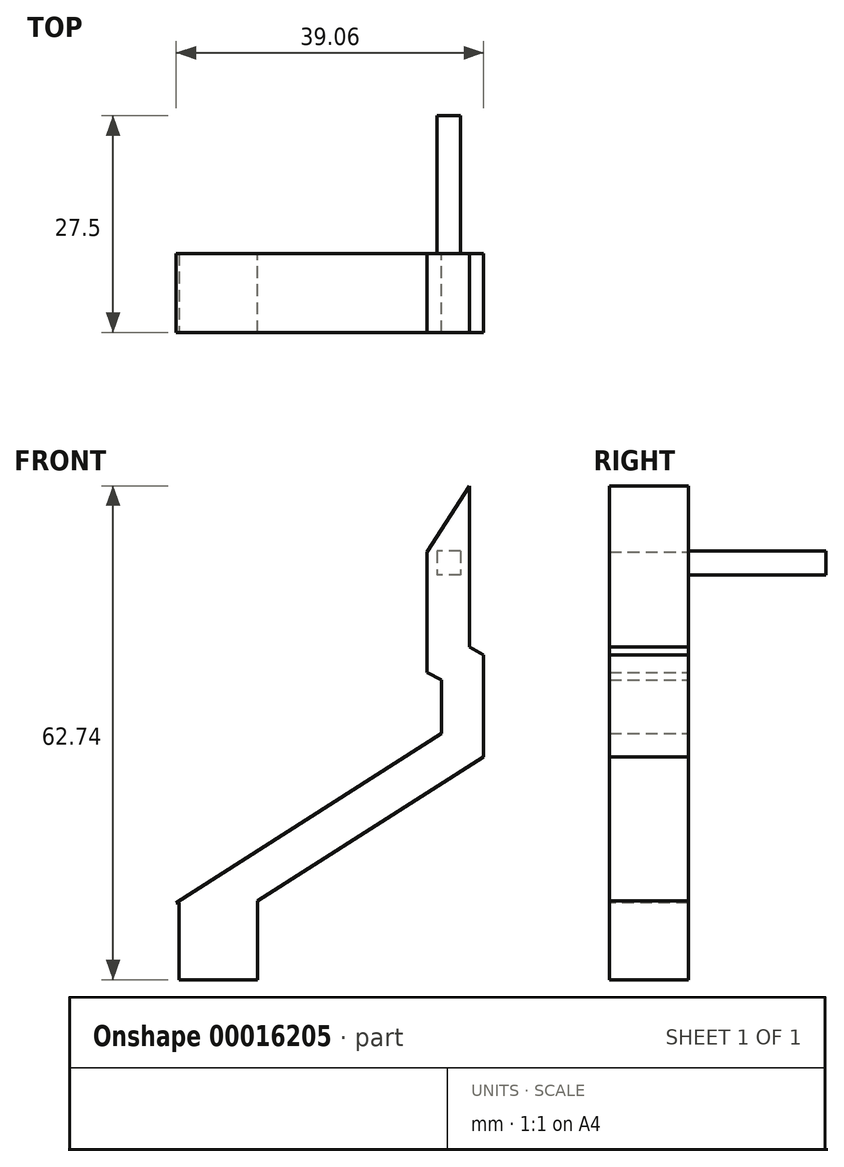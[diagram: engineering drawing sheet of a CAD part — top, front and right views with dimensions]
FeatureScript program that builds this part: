
annotation { "Feature Type Name" : "Feature", "Feature Type Description" : "" }
export const myFeature = defineFeature(function(context is Context, id is Id, definition is map)
    precondition{}
    {
        {
            var Q0;
            Q0=qCreatedBy(makeId("Right.planeOp"),FACE);
            var sketch = newSketch(context, id + "F0", { "sketchPlane" : qUnion([Q0])});
            skLineSegment(sketch, "E0.bottom", {"start": v(-13.57, -10.67) * mm, "end": v(-3.57, -10.67) * mm});
            skLineSegment(sketch, "E0.top", {"start": v(-13.57, -20.67) * mm, "end": v(-3.57, -20.67) * mm});
            skLineSegment(sketch, "E0.left", {"start": v(-13.57, -10.67) * mm, "end": v(-13.57, -20.67) * mm});
            skLineSegment(sketch, "E0.right", {"start": v(-3.57, -10.67) * mm, "end": v(-3.57, -20.67) * mm});
            skSolve(sketch);
        }
        {
            var Q0;
            Q0=makeQuery(id+"F0.imprint","IMPRINT",FACE,{"disambiguationData":[TD([[makeQuery(id+"F0.imprint","IMPRINT",EDGE,{"derivedFrom":sQuery(id+"F0.wireOp",EDGE,"E0.bottom")}),-1.0]])]});
            extrude(context, id + "F1", {"entities" : qUnion([Q0]), "depth" : 10 * mm});
        }
        {
            var Q0;
            Q0=makeQuery(id+"F1.opExtrude","SWEPT_FACE",FACE,{"disambiguationData":[OSD([sQuery(id+"F0.wireOp",EDGE,"E0.bottom")])]});
            var sketch = newSketch(context, id + "F2", { "sketchPlane" : qUnion([Q0])});
            skLineSegment(sketch, "E1.bottom", {"start": v(0, -3.57) * mm, "end": v(10, -3.57) * mm});
            skLineSegment(sketch, "E1.top", {"start": v(0, -13.57) * mm, "end": v(10, -13.57) * mm});
            skLineSegment(sketch, "E1.left", {"start": v(0, -3.57) * mm, "end": v(0, -13.57) * mm});
            skLineSegment(sketch, "E1.right", {"start": v(10, -3.57) * mm, "end": v(10, -13.57) * mm});
            skSolve(sketch);
        }
        {
            var Q0;
            Q0=qCreatedBy(makeId("Front.planeOp"),FACE);
            var sketch = newSketch(context, id + "F3", { "sketchPlane" : qUnion([Q0])});
            skLineSegment(sketch, "E2", {"start": v(4.82, -10.91) * mm, "end": v(36.1, 9.06) * mm});
            skLineSegment(sketch, "E3", {"start": v(36.1, 9.06) * mm, "end": v(36.1, 19.06) * mm});
            skLineSegment(sketch, "E4", {"start": v(36.1, 19.06) * mm, "end": v(34.3, 20.02) * mm});
            skLineSegment(sketch, "E5", {"start": v(34.3, 20.02) * mm, "end": v(34.3, 38.02) * mm});
            skSolve(sketch);
        }
        {
            var Q0;
            Q0=makeQuery(id+"F2.imprint","IMPRINT",FACE,{"disambiguationData":[TD([[makeQuery(id+"F2.imprint","IMPRINT",EDGE,{"derivedFrom":sQuery(id+"F2.wireOp",EDGE,"E1.bottom")}),1.0]])]});
            var Q1;
            Q1=sQuery(id+"F3.wireOp",EDGE,"E5");
            var Q2;
            Q2=sQuery(id+"F3.wireOp",EDGE,"E2");
            var Q3;
            Q3=sQuery(id+"F3.wireOp",EDGE,"E4");
            var Q4;
            Q4=sQuery(id+"F3.wireOp",EDGE,"E3");
            sweep(context, id + "F4", {"operationType" : NewBodyOperationType.ADD, "profiles" : qUnion([Q0]), "path" : qUnion([Q1, Q2, Q3, Q4])});
        }
        {
            var Q0;
            Q0=makeQuery(id+"F4.boolean.opBoolean","MERGE",FACE,{"derivedFrom":[makeQuery(id+"F1.opExtrude","SWEPT_FACE",FACE,{"disambiguationData":[OSD([sQuery(id+"F0.wireOp",EDGE,"E0.right")])]}),makeQuery(id+"F4.opSweep","SWEPT_FACE",FACE,{"disambiguationData":[OSD([sQuery(id+"F2.wireOp",EDGE,"E1.bottom"),sQuery(id+"F3.wireOp",EDGE,"E2")])]})]});
            var sketch = newSketch(context, id + "F5", { "sketchPlane" : qUnion([Q0])});
            skLineSegment(sketch, "E6.bottom", {"start": v(-35.78, 33.77) * mm, "end": v(-32.78, 33.77) * mm});
            skLineSegment(sketch, "E6.top", {"start": v(-35.78, 30.77) * mm, "end": v(-32.78, 30.77) * mm});
            skLineSegment(sketch, "E6.left", {"start": v(-35.78, 33.77) * mm, "end": v(-35.78, 30.77) * mm});
            skLineSegment(sketch, "E6.right", {"start": v(-32.78, 33.77) * mm, "end": v(-32.78, 30.77) * mm});
            skSolve(sketch);
        }
        {
            var Q0;
            Q0=makeQuery(id+"F5.imprint","IMPRINT",FACE,{"disambiguationData":[TD([[makeQuery(id+"F5.imprint","IMPRINT",EDGE,{"derivedFrom":sQuery(id+"F5.wireOp",EDGE,"E6.bottom")}),-1.0]])]});
            extrude(context, id + "F6", {"entities" : qUnion([Q0]), "operationType" : NewBodyOperationType.ADD, "depth" : 17.5 * mm});
        }
    });
